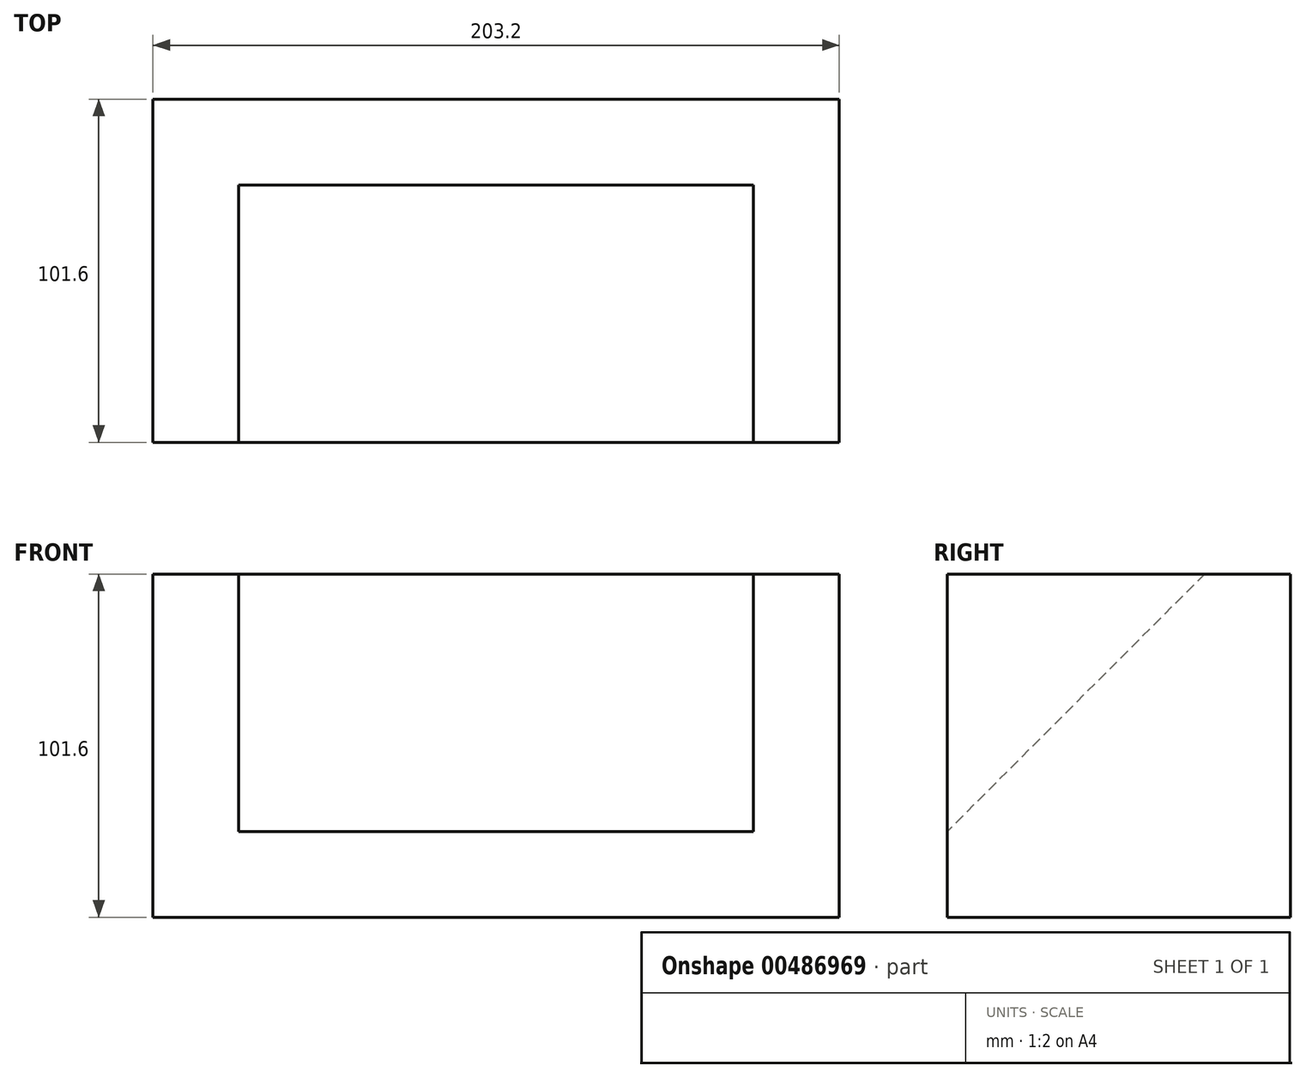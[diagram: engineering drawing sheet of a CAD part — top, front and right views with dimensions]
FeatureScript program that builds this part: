
annotation { "Feature Type Name" : "Feature", "Feature Type Description" : "" }
export const myFeature = defineFeature(function(context is Context, id is Id, definition is map)
    precondition{}
    {
        {
            var Q0;
            Q0=qCreatedBy(makeId("Front.planeOp"),FACE);
            var sketch = newSketch(context, id + "F0", { "sketchPlane" : qUnion([Q0])});
            skLineSegment(sketch, "E0.bottom", {"start": v(0, 0) * mm, "end": v(-203.2, 0) * mm});
            skLineSegment(sketch, "E0.top", {"start": v(0, 101.6) * mm, "end": v(-203.2, 101.6) * mm});
            skLineSegment(sketch, "E0.left", {"start": v(0, 0) * mm, "end": v(0, 101.6) * mm});
            skLineSegment(sketch, "E0.right", {"start": v(-203.2, 0) * mm, "end": v(-203.2, 101.6) * mm});
            skSolve(sketch);
        }
        {
            var Q0;
            Q0=makeQuery(id+"F0.imprint","IMPRINT",FACE,{"disambiguationData":[TD([[makeQuery(id+"F0.imprint","IMPRINT",EDGE,{"derivedFrom":sQuery(id+"F0.wireOp",EDGE,"E0.bottom")}),-1.0]])]});
            extrude(context, id + "F1", {"entities" : qUnion([Q0]), "depth" : 101.6 * mm});
        }
        {
            var Q0;
            Q0=makeQuery(id+"F1.opExtrude","CAP_FACE",FACE,{"disambiguationData":[OSD([sQuery(id+"F0.wireOp",EDGE,"E0.bottom"),sQuery(id+"F0.wireOp",EDGE,"E0.top"),sQuery(id+"F0.wireOp",EDGE,"E0.left"),sQuery(id+"F0.wireOp",EDGE,"E0.right")])],"isStart":false});
            var sketch = newSketch(context, id + "F2", { "sketchPlane" : qUnion([Q0])});
            skLineSegment(sketch, "E1.bottom", {"start": v(-177.8, 0) * mm, "end": v(-25.4, 0) * mm});
            skLineSegment(sketch, "E1.top", {"start": v(-177.8, 76.2) * mm, "end": v(-25.4, 76.2) * mm});
            skLineSegment(sketch, "E1.left", {"start": v(-177.8, 0) * mm, "end": v(-177.8, 76.2) * mm});
            skLineSegment(sketch, "E1.right", {"start": v(-25.4, 0) * mm, "end": v(-25.4, 76.2) * mm});
            skSolve(sketch);
        }
        {
            var Q0;
            Q0=makeQuery(id+"F2.imprint","IMPRINT",FACE,{"disambiguationData":[TD([[makeQuery(id+"F2.imprint","IMPRINT",EDGE,{"derivedFrom":sQuery(id+"F2.wireOp",EDGE,"E1.bottom")}),-1.0]])]});
            extrude(context, id + "F3", {"entities" : qUnion([Q0]), "operationType" : NewBodyOperationType.REMOVE, "oppositeDirection" : true, "depth" : 76.2 * mm});
        }
        {
            var Q0;
            Q0=makeQuery(id+"F3.boolean.opBoolean","COPY",FACE,{"derivedFrom":makeQuery(id+"F3.opExtrude","SWEPT_FACE",FACE,{"disambiguationData":[OSD([sQuery(id+"F2.wireOp",EDGE,"E1.left")])]})});
            var sketch = newSketch(context, id + "F4", { "sketchPlane" : qUnion([Q0])});
            skLineSegment(sketch, "E2", {"start": v(-101.6, 76.2) * mm, "end": v(-25.4, 0) * mm});
            skLineSegment(sketch, "E3", {"start": v(-25.4, 0) * mm, "end": v(-25.4, 76.2) * mm});
            skLineSegment(sketch, "E4", {"start": v(-25.4, 76.2) * mm, "end": v(-101.6, 76.2) * mm});
            skSolve(sketch);
        }
        {
            var Q0;
            Q0=makeQuery(id+"F4.imprint","IMPRINT",FACE,{"disambiguationData":[TD([[makeQuery(id+"F4.imprint","IMPRINT",EDGE,{"derivedFrom":sQuery(id+"F4.wireOp",EDGE,"E2")}),1.0]])]});
            extrude(context, id + "F5", {"entities" : qUnion([Q0]), "operationType" : NewBodyOperationType.ADD, "depth" : 152.4 * mm});
        }
        {
            var Q0;
            Q0=makeQuery(id+"F1.opExtrude","SWEPT_BODY",BODY,{"disambiguationData":[OSD([sQuery(id+"F0.wireOp",EDGE,"E0.bottom"),sQuery(id+"F0.wireOp",EDGE,"E0.top"),sQuery(id+"F0.wireOp",EDGE,"E0.left"),sQuery(id+"F0.wireOp",EDGE,"E0.right")])]});
            var Q1;
            Q1=makeQuery(id+"F1.opExtrude","CAP_EDGE",EDGE,{"disambiguationData":[OSD([sQuery(id+"F0.wireOp",EDGE,"E0.top")])],"isStart":true});
            transform(context, id + "F6", {"entities" : qUnion([Q0]), "transformType" : TransformType.ROTATION, "transformAxis" : qUnion([Q1]), "angle" : 90 * degree, "makeCopy" : false});
        }
    });
